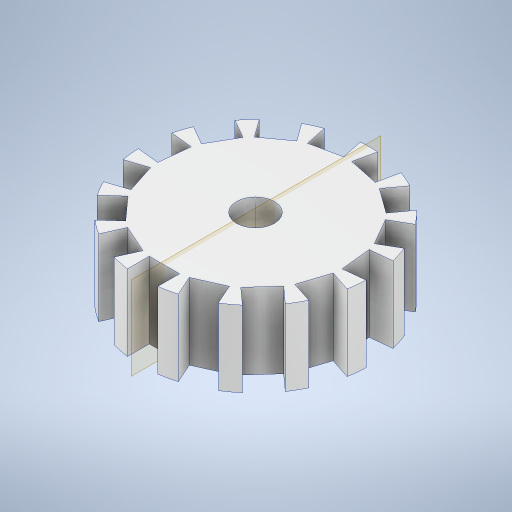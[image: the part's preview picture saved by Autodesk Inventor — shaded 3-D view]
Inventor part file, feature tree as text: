
AUTODESK INVENTOR PART (.ipt)
format: ipt  version: 2023 (Build 270158000, 158)  size: 323,072 bytes
history: native  units: mm
features: sketch x3, extrude x3, plane x1, pattern_circular x1, chamfer x1
ambient origin geometry x8: Origin, YZ Plane, XZ Plane, XY Plane, X Axis, Y Axis, Z Axis, Center Point
bodies: Solid1 (feature_tree)
feature tree (9):
  sketch  "Sketch1"  dims[d0=30.0mm d1=10.0mm d2=10.0mm d3=0.0mm]
  plane  "Work Plane1"
  extrude  "Extrusion1"  Depth=10.0mm TaperAngle=0.0deg
  extrude  "Extrusion2"  Depth=10.0mm
  pattern_circular  "Circular Pattern1"  [2 undecoded]
  extrude  "Extrusion6"  Depth=10.0mm TaperAngle=360.0deg
  chamfer  "Chamfer1"  Distance=5.0mm
  sketch  "Sketch2"  dims[d4=4.0mm d5=10.0mm]
  sketch  "Sketch6"  dims[d6=12.0mm d7=10.0mm d8=0.0mm d9=150.0mm d10=360.0deg d24=5.0mm d25=10.0mm d26=0.0mm d27=1.0mm d28=2.0mm d29=45.0deg]
note: 2 required parameter values undecoded (feature->parameter linkage not recoverable at this tier; creation-order binding heuristic only, values carry confidence <= 0.55)
